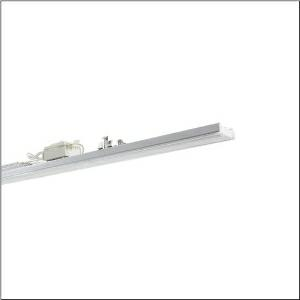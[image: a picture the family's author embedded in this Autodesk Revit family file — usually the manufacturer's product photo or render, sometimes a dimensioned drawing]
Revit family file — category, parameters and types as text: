
# Revit family: licross_r__21_recessed_ho_52tl12dv4lxm_44ad
name_source: partatom
category: Lighting Fixtures
units: mm (PartAtom-declared; Revit-internal decimal feet)

## family parameters
Cut with Voids When Loaded = No
Host = Face
Light Source = No
Part Type = Normal
Room Calculation Point = No
Round Connector Dimension = Use Diameter
Shared = No

## types (1)
- --- (1 x LED, 20000 lm, 109.8 W, 4000K)
    Apparent Load = 110 VA
    CIE Flux Codes = 69 91 98 100 100
    Color Rendering = 80
    Color Temperature = 4000K
    Default Elevation = 1800 mm
    Description = Licross® 21 Recessed HO, luminaire insert, of sheet steel, galvanised, coil coated, white, length: 2.250mm, width: 66mm, height: 67mm, LED rated luminous flux: 20.000lm, light colour: 840, control gear: DALI 2, with plug, 5-pole, with phase selection, mains connection: 220..240V, AC, 50/60Hz, rated input power: 110W, halogen-free wiring, primary optical cover: cover, of PMMA, light emission: direct distribution, primary light characteristic: symmetric, protection rating (complete): IP40, insulation class (complete): insulation class I (protective earthing), certification: CE, ENEC, VDE, UKCA, protection symbol: D if used in an environment without relevant dust loads with corresponding accessories, impact resistance: IK06, permissible ambient temperature for indoor applications: -40..+35°C, corresponds to IFS (International Featured Standards) requirements for safety and quality in the food industry, reducing of maximum allowable ambient temperature of 5°C with ceiling mounting, LABS conformity tested according to VDMA 24364:2018-05, packaging unit: 1 piece
    Height = 58 mm
    Lamp = 1 x LED
    Lamp Light Flux = 20000 lm
    Lamp Power = 109.8 W
    Lamp count = 1
    Length = 2250 mm
    Luminous efficacy = 182 lm/W
    Manufacturer = Siteco
    ModVariant = No
    Model = 52TL12DV4LXM
    Mounting Place = Ceiling
    Mounting Type = Pendant
    Number of Poles = 1
    OnlyDefault = Yes
    Power Factor = 1
    Product Name = Licross® 21 Recessed HO
    Product group = luminaire insert
    ProductGroupID = 902
    Protection Class = Protection class I
    Protection Degree = IP 40
    RLX_Detail_Level = 1
    RLX_Emergency_Light_Flux = 0 lm
    RLX_Emergency_Type = 0
    RLX_Emergency_Type_DB = No
    RlxData = <blob elided: 29753 chars, md5=6d7e948e>
    Socket = socket
    Standby Power = 0 W
    System Light Flux = 20000 lm
    System Power = 110 W
    Type Comments = factory setting: luminous flux: 100 % | dim-lin: 254 | 425 mA
    Type Image = l_1296930.jpg
    URL = http://relux.com
    VarID = @adj_116684
    Voltage = 0 V
    Weight = 0.00 kg
    Width = 66 mm

## geometry (parser evidence)
native form markers: Blend x4, Sweep x9
no freeform markers — native parametric forms only
